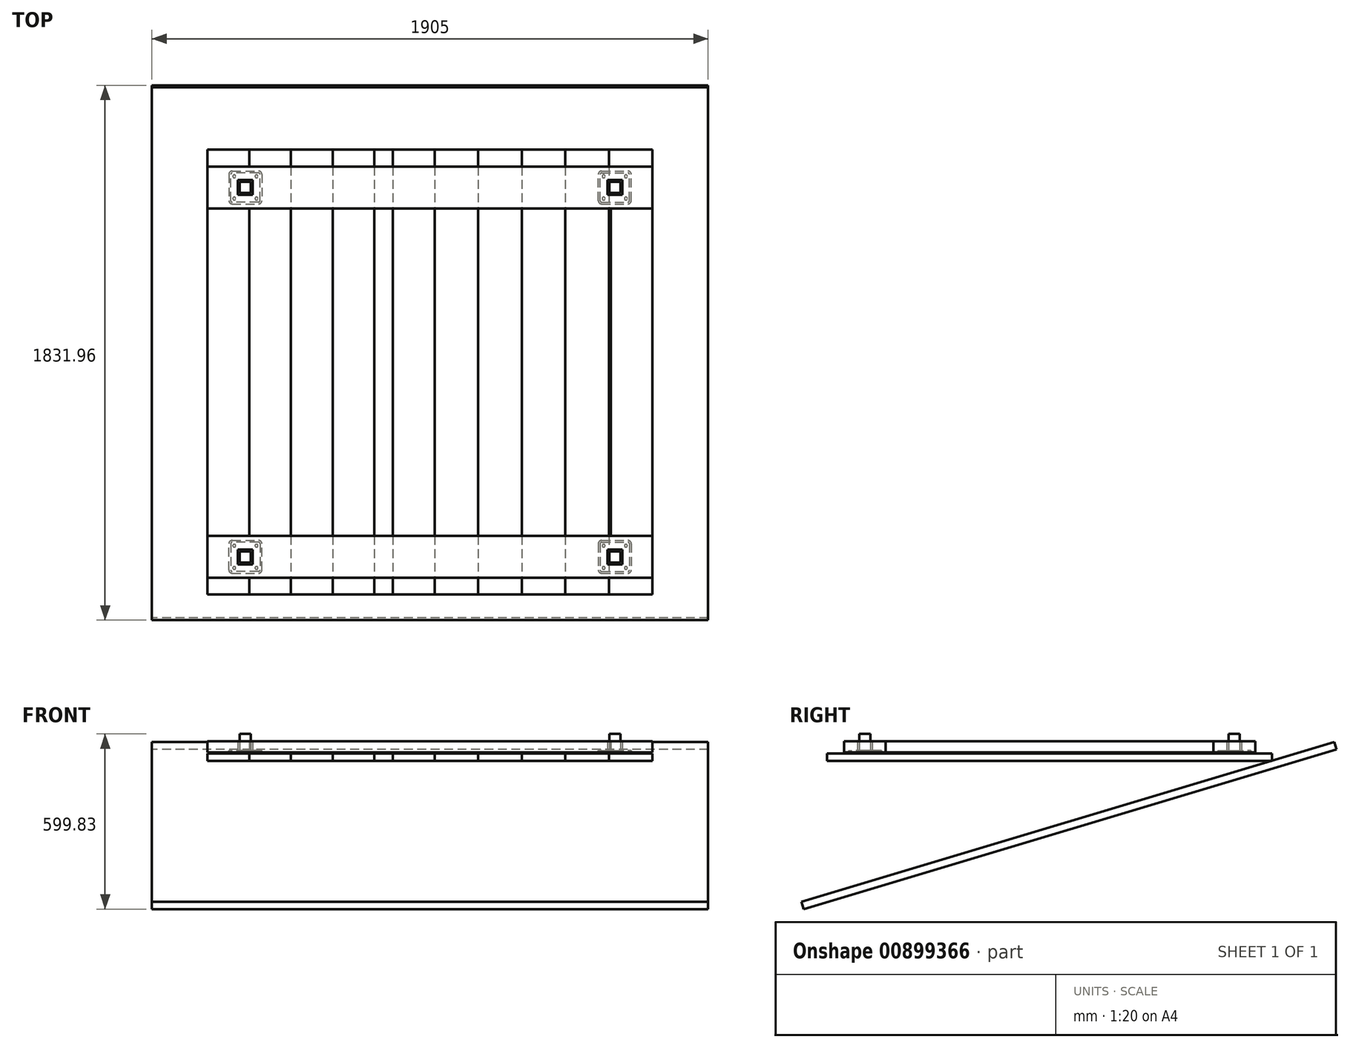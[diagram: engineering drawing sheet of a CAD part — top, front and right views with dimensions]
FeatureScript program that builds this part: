
annotation { "Feature Type Name" : "Feature", "Feature Type Description" : "" }
export const myFeature = defineFeature(function(context is Context, id is Id, definition is map)
    precondition{}
    {
        {
            var Q0;
            Q0=qCreatedBy(makeId("Top.planeOp"),FACE);
            var sketch = newSketch(context, id + "F0", { "sketchPlane" : qUnion([Q0])});
            skLineSegment(sketch, "E0.bottom", {"start": v(762, -762) * mm, "end": v(-762, -762) * mm});
            skLineSegment(sketch, "E0.top", {"start": v(762, 762) * mm, "end": v(-762, 762) * mm});
            skLineSegment(sketch, "E0.left", {"start": v(762, -762) * mm, "end": v(762, 762) * mm});
            skLineSegment(sketch, "E0.right", {"start": v(-762, -762) * mm, "end": v(-762, 762) * mm});
            skPoint(sketch, "E0.middle", {"position": v(0, 0) * mm});
            skLineSegment(sketch, "E1", {"start": v(-619.13, 762) * mm, "end": v(-619.13, -762) * mm});
            skLineSegment(sketch, "E2", {"start": v(612.78, 762) * mm, "end": v(612.78, -762) * mm});
            skLineSegment(sketch, "E3", {"start": v(-476.25, 762) * mm, "end": v(-476.25, -762) * mm});
            skLineSegment(sketch, "E4", {"start": v(-333.38, 762) * mm, "end": v(-333.38, -762) * mm});
            skLineSegment(sketch, "E5", {"start": v(-190.5, 762) * mm, "end": v(-190.5, -762) * mm});
            skLineSegment(sketch, "E6", {"start": v(-127, 762) * mm, "end": v(-127, -762) * mm});
            skLineSegment(sketch, "E7", {"start": v(463.55, 762) * mm, "end": v(463.55, -762) * mm});
            skLineSegment(sketch, "E8", {"start": v(314.33, 762) * mm, "end": v(314.33, -762) * mm});
            skLineSegment(sketch, "E9", {"start": v(165.1, 762) * mm, "end": v(165.1, -762) * mm});
            skLineSegment(sketch, "E10", {"start": v(15.88, 762) * mm, "end": v(15.88, -762) * mm});
            skSolve(sketch);
        }
        {
            var Q0;
            Q0=qCreatedBy(makeId("Right.planeOp"),FACE);
            var sketch = newSketch(context, id + "F1", { "sketchPlane" : qUnion([Q0])});
            skLineSegment(sketch, "E11", {"start": v(762, 0) * mm, "end": v(-762, -457.2) * mm});
            skSolve(sketch);
        }
        {
            var Q0;
            Q0=sQuery(id+"F1.wireOp",EDGE,"E11");
            cPlane(context, id + "F2", {"entities" : qUnion([Q0]), "cplaneType" : CPlaneType.LINE_ANGLE, "offset" : 25.4 * mm, "angle" : 0 * degree, "width" : 152.4 * mm, "height" : 152.4 * mm});
        }
        {
            var Q0;
            Q0=qCreatedBy(id+"F2.planeOp",FACE);
            var sketch = newSketch(context, id + "F3", { "sketchPlane" : qUnion([Q0])});
            skLineSegment(sketch, "E12.bottom", {"start": v(952.5, 952.5) * mm, "end": v(-952.5, 952.5) * mm});
            skLineSegment(sketch, "E12.top", {"start": v(952.5, -952.5) * mm, "end": v(-952.5, -952.5) * mm});
            skLineSegment(sketch, "E12.left", {"start": v(952.5, 952.5) * mm, "end": v(952.5, -952.5) * mm});
            skLineSegment(sketch, "E12.right", {"start": v(-952.5, 952.5) * mm, "end": v(-952.5, -952.5) * mm});
            skPoint(sketch, "E12.middle", {"position": v(0, 0) * mm});
            skSolve(sketch);
        }
        {
            var Q0;
            Q0=makeQuery(id+"F3.imprint","IMPRINT",FACE,{"disambiguationData":[TD([[makeQuery(id+"F3.imprint","IMPRINT",EDGE,{"derivedFrom":sQuery(id+"F3.wireOp",EDGE,"E12.bottom")}),1.0]])]});
            extrude(context, id + "F4", {"entities" : qUnion([Q0]), "depth" : 25.4 * mm, "offsetDistance" : 25.4 * mm});
        }
        {
            var Q0;
            {var subQ0=sQuery(id+"F0.wireOp",EDGE,"E1");Q0=makeQuery(id+"F0.imprint","IMPRINT",FACE,{"disambiguationData":[TD([[makeQuery(id+"F0.imprint","IMPRINT",EDGE,{"derivedFrom":subQ0}),1.0]])]});}
            var Q1;
            {var subQ0=sQuery(id+"F0.wireOp",EDGE,"E4");Q1=makeQuery(id+"F0.imprint","IMPRINT",FACE,{"disambiguationData":[TD([[makeQuery(id+"F0.imprint","IMPRINT",EDGE,{"derivedFrom":subQ0}),1.0]])]});}
            var Q2;
            {var subQ0=sQuery(id+"F0.wireOp",EDGE,"E6");Q2=makeQuery(id+"F0.imprint","IMPRINT",FACE,{"disambiguationData":[TD([[makeQuery(id+"F0.imprint","IMPRINT",EDGE,{"derivedFrom":subQ0}),1.0]])]});}
            var Q3;
            {var subQ0=sQuery(id+"F0.wireOp",EDGE,"E8");Q3=makeQuery(id+"F0.imprint","IMPRINT",FACE,{"disambiguationData":[TD([[makeQuery(id+"F0.imprint","IMPRINT",EDGE,{"derivedFrom":subQ0}),-1.0]])]});}
            var Q4;
            {var subQ0=sQuery(id+"F0.wireOp",EDGE,"E2");Q4=makeQuery(id+"F0.imprint","IMPRINT",FACE,{"disambiguationData":[TD([[makeQuery(id+"F0.imprint","IMPRINT",EDGE,{"derivedFrom":subQ0}),-1.0]])]});}
            extrude(context, id + "F5", {"entities" : qUnion([Q0, Q1, Q2, Q3, Q4]), "depth" : 25.4 * mm, "offsetDistance" : 25.4 * mm});
        }
        {
            var Q0;
            {var subQ0=sQuery(id+"F0.wireOp",EDGE,"E0.right");Q0=makeQuery(id+"F0.imprint","IMPRINT",FACE,{"disambiguationData":[TD([[makeQuery(id+"F0.imprint","IMPRINT",EDGE,{"derivedFrom":subQ0}),-1.0]])]});}
            var Q1;
            {var subQ0=sQuery(id+"F0.wireOp",EDGE,"E3");Q1=makeQuery(id+"F0.imprint","IMPRINT",FACE,{"disambiguationData":[TD([[makeQuery(id+"F0.imprint","IMPRINT",EDGE,{"derivedFrom":subQ0}),1.0]])]});}
            var Q2;
            {var subQ0=sQuery(id+"F0.wireOp",EDGE,"E5");Q2=makeQuery(id+"F0.imprint","IMPRINT",FACE,{"disambiguationData":[TD([[makeQuery(id+"F0.imprint","IMPRINT",EDGE,{"derivedFrom":subQ0}),1.0]])]});}
            var Q3;
            {var subQ0=sQuery(id+"F0.wireOp",EDGE,"E9");Q3=makeQuery(id+"F0.imprint","IMPRINT",FACE,{"disambiguationData":[TD([[makeQuery(id+"F0.imprint","IMPRINT",EDGE,{"derivedFrom":subQ0}),-1.0]])]});}
            var Q4;
            {var subQ0=sQuery(id+"F0.wireOp",EDGE,"E7");Q4=makeQuery(id+"F0.imprint","IMPRINT",FACE,{"disambiguationData":[TD([[makeQuery(id+"F0.imprint","IMPRINT",EDGE,{"derivedFrom":subQ0}),-1.0]])]});}
            var Q5;
            {var subQ0=sQuery(id+"F0.wireOp",EDGE,"E0.left");Q5=makeQuery(id+"F0.imprint","IMPRINT",FACE,{"disambiguationData":[TD([[makeQuery(id+"F0.imprint","IMPRINT",EDGE,{"derivedFrom":subQ0}),1.0]])]});}
            extrude(context, id + "F6", {"entities" : qUnion([Q0, Q1, Q2, Q3, Q4, Q5]), "depth" : 25.4 * mm, "offsetDistance" : 25.4 * mm});
        }
        {
            var Q0;
            Q0=qCreatedBy(makeId("Top.planeOp"),FACE);
            cPlane(context, id + "F7", {"entities" : qUnion([Q0]), "cplaneType" : CPlaneType.OFFSET, "offset" : 25.4 * mm, "width" : 152.4 * mm, "height" : 152.4 * mm});
        }
        {
            var Q0;
            Q0=qCreatedBy(id+"F7.planeOp",FACE);
            var sketch = newSketch(context, id + "F8", { "sketchPlane" : qUnion([Q0])});
            skLineSegment(sketch, "E13", {"start": v(-889.17, 0) * mm, "end": v(880.99, 0) * mm, "construction": true});
            skLineSegment(sketch, "E14", {"start": v(0, 851.29) * mm, "end": v(0, -881.65) * mm, "construction": true});
            skLineSegment(sketch, "E15.bottom", {"start": v(-587.38, 582.61) * mm, "end": v(-677.86, 582.61) * mm});
            skLineSegment(sketch, "E15.top", {"start": v(-587.38, 682.62) * mm, "end": v(-677.86, 682.62) * mm});
            skLineSegment(sketch, "E15.left", {"start": v(-582.61, 587.38) * mm, "end": v(-582.61, 677.86) * mm});
            skLineSegment(sketch, "E15.right", {"start": v(-682.62, 587.38) * mm, "end": v(-682.62, 677.86) * mm});
            skPoint(sketch, "E15.middle", {"position": v(-632.62, 632.62) * mm});
            skPoint(sketch, "E16.visualSharp", {"position": v(-682.62, 682.62) * mm});
            skArc(sketch, "E16.filletArc", {"start": v(-677.86, 682.62) * mm, "mid": v(-681.23, 681.23) * mm, "end": v(-682.62, 677.86) * mm});
            skPoint(sketch, "E17.visualSharp", {"position": v(-582.61, 682.62) * mm});
            skArc(sketch, "E17.filletArc", {"start": v(-582.61, 677.86) * mm, "mid": v(-584, 681.23) * mm, "end": v(-587.38, 682.62) * mm});
            skPoint(sketch, "E18.visualSharp", {"position": v(-582.61, 582.61) * mm});
            skArc(sketch, "E18.filletArc", {"start": v(-587.38, 582.61) * mm, "mid": v(-584, 584) * mm, "end": v(-582.61, 587.38) * mm});
            skPoint(sketch, "E19.visualSharp", {"position": v(-682.62, 582.61) * mm});
            skArc(sketch, "E19.filletArc", {"start": v(-682.62, 587.38) * mm, "mid": v(-681.23, 584) * mm, "end": v(-677.86, 582.61) * mm});
            skCircle(sketch, "E20", {"center": v(-670.72, 670.72) * mm, "radius": 5.08 * mm});
            skCircle(sketch, "E21", {"center": v(-594.52, 670.72) * mm, "radius": 5.08 * mm});
            skCircle(sketch, "E22", {"center": v(-594.52, 594.52) * mm, "radius": 5.08 * mm});
            skCircle(sketch, "E23", {"center": v(-670.72, 594.52) * mm, "radius": 5.08 * mm});
            skLineSegment(sketch, "E24", {"start": v(-686.43, 632.62) * mm, "end": v(-578.8, 632.62) * mm, "construction": true});
            skLineSegment(sketch, "E25", {"start": v(-632.62, 682.62) * mm, "end": v(-632.62, 582.61) * mm, "construction": true});
            skLineSegment(sketch, "E26", {"start": v(-670.72, 594.52) * mm, "end": v(-594.52, 594.52) * mm, "construction": true});
            skLineSegment(sketch, "E27", {"start": v(-670.72, 594.52) * mm, "end": v(-670.72, 670.72) * mm, "construction": true});
            skPoint(sketch, "E28", {"position": v(-670.72, 632.62) * mm});
            skPoint(sketch, "E29", {"position": v(-632.62, 594.52) * mm});
            skLineSegment(sketch, "E30", {"start": v(-632.62, -632.62) * mm, "end": v(632.62, -632.62) * mm, "construction": true});
            skLineSegment(sketch, "E31.bottom", {"start": v(677.86, 582.61) * mm, "end": v(587.38, 582.61) * mm});
            skLineSegment(sketch, "E31.top", {"start": v(677.86, 682.62) * mm, "end": v(587.38, 682.62) * mm});
            skLineSegment(sketch, "E31.left", {"start": v(682.63, 587.38) * mm, "end": v(682.63, 677.86) * mm});
            skLineSegment(sketch, "E31.right", {"start": v(582.61, 587.38) * mm, "end": v(582.61, 677.86) * mm});
            skPoint(sketch, "E31.middle", {"position": v(632.62, 632.62) * mm});
            skPoint(sketch, "E32.visualSharp", {"position": v(582.61, 682.62) * mm});
            skArc(sketch, "E32.filletArc", {"start": v(587.38, 682.62) * mm, "mid": v(584, 681.23) * mm, "end": v(582.61, 677.86) * mm});
            skPoint(sketch, "E33.visualSharp", {"position": v(682.63, 682.62) * mm});
            skArc(sketch, "E33.filletArc", {"start": v(682.63, 677.86) * mm, "mid": v(681.23, 681.23) * mm, "end": v(677.86, 682.62) * mm});
            skPoint(sketch, "E34.visualSharp", {"position": v(682.63, 582.61) * mm});
            skArc(sketch, "E34.filletArc", {"start": v(677.86, 582.61) * mm, "mid": v(681.23, 584) * mm, "end": v(682.63, 587.38) * mm});
            skPoint(sketch, "E35.visualSharp", {"position": v(582.61, 582.61) * mm});
            skArc(sketch, "E35.filletArc", {"start": v(582.61, 587.38) * mm, "mid": v(584, 584) * mm, "end": v(587.38, 582.61) * mm});
            skCircle(sketch, "E36", {"center": v(594.52, 670.72) * mm, "radius": 5.08 * mm});
            skCircle(sketch, "E37", {"center": v(670.72, 670.72) * mm, "radius": 5.08 * mm});
            skCircle(sketch, "E38", {"center": v(670.72, 594.52) * mm, "radius": 5.08 * mm});
            skCircle(sketch, "E39", {"center": v(594.52, 594.52) * mm, "radius": 5.08 * mm});
            skLineSegment(sketch, "E40", {"start": v(582.61, 632.62) * mm, "end": v(682.62, 632.62) * mm, "construction": true});
            skLineSegment(sketch, "E41", {"start": v(632.62, 682.62) * mm, "end": v(632.62, 582.61) * mm, "construction": true});
            skLineSegment(sketch, "E42", {"start": v(594.52, 594.52) * mm, "end": v(670.72, 594.52) * mm, "construction": true});
            skLineSegment(sketch, "E43", {"start": v(594.52, 594.52) * mm, "end": v(594.52, 670.72) * mm, "construction": true});
            skPoint(sketch, "E44", {"position": v(594.52, 632.62) * mm});
            skPoint(sketch, "E45", {"position": v(632.62, 594.52) * mm});
            skLineSegment(sketch, "E46.bottom", {"start": v(-587.38, -682.62) * mm, "end": v(-677.86, -682.62) * mm});
            skLineSegment(sketch, "E46.top", {"start": v(-587.38, -582.61) * mm, "end": v(-677.86, -582.61) * mm});
            skLineSegment(sketch, "E46.left", {"start": v(-582.61, -677.86) * mm, "end": v(-582.61, -587.38) * mm});
            skLineSegment(sketch, "E46.right", {"start": v(-682.62, -677.86) * mm, "end": v(-682.62, -587.38) * mm});
            skPoint(sketch, "E46.middle", {"position": v(-632.62, -632.62) * mm});
            skPoint(sketch, "E47.visualSharp", {"position": v(-682.62, -582.61) * mm});
            skArc(sketch, "E47.filletArc", {"start": v(-677.86, -582.61) * mm, "mid": v(-681.23, -584) * mm, "end": v(-682.62, -587.38) * mm});
            skPoint(sketch, "E48.visualSharp", {"position": v(-582.61, -582.61) * mm});
            skArc(sketch, "E48.filletArc", {"start": v(-582.61, -587.38) * mm, "mid": v(-584, -584) * mm, "end": v(-587.38, -582.61) * mm});
            skPoint(sketch, "E49.visualSharp", {"position": v(-582.61, -682.62) * mm});
            skArc(sketch, "E49.filletArc", {"start": v(-587.38, -682.62) * mm, "mid": v(-584, -681.23) * mm, "end": v(-582.61, -677.86) * mm});
            skPoint(sketch, "E50.visualSharp", {"position": v(-682.62, -682.62) * mm});
            skArc(sketch, "E50.filletArc", {"start": v(-682.62, -677.86) * mm, "mid": v(-681.23, -681.23) * mm, "end": v(-677.86, -682.62) * mm});
            skCircle(sketch, "E51", {"center": v(-670.72, -594.52) * mm, "radius": 5.08 * mm});
            skCircle(sketch, "E52", {"center": v(-594.52, -594.52) * mm, "radius": 5.08 * mm});
            skCircle(sketch, "E53", {"center": v(-594.52, -670.72) * mm, "radius": 5.08 * mm});
            skCircle(sketch, "E54", {"center": v(-670.72, -670.72) * mm, "radius": 5.08 * mm});
            skLineSegment(sketch, "E55", {"start": v(-682.62, -632.62) * mm, "end": v(-582.61, -632.62) * mm, "construction": true});
            skLineSegment(sketch, "E56", {"start": v(-632.62, -582.61) * mm, "end": v(-632.62, -682.62) * mm, "construction": true});
            skLineSegment(sketch, "E57", {"start": v(-670.72, -670.72) * mm, "end": v(-594.52, -670.72) * mm, "construction": true});
            skLineSegment(sketch, "E58", {"start": v(-670.72, -670.72) * mm, "end": v(-670.72, -594.52) * mm, "construction": true});
            skPoint(sketch, "E59", {"position": v(-670.72, -632.62) * mm});
            skPoint(sketch, "E60", {"position": v(-632.62, -670.72) * mm});
            skLineSegment(sketch, "E61.bottom", {"start": v(677.86, -682.62) * mm, "end": v(587.38, -682.62) * mm});
            skLineSegment(sketch, "E61.top", {"start": v(677.86, -582.61) * mm, "end": v(587.38, -582.61) * mm});
            skLineSegment(sketch, "E61.left", {"start": v(682.62, -677.86) * mm, "end": v(682.62, -587.38) * mm});
            skLineSegment(sketch, "E61.right", {"start": v(582.61, -677.86) * mm, "end": v(582.61, -587.38) * mm});
            skPoint(sketch, "E61.middle", {"position": v(632.62, -632.62) * mm});
            skPoint(sketch, "E62.visualSharp", {"position": v(582.61, -582.61) * mm});
            skArc(sketch, "E62.filletArc", {"start": v(587.38, -582.61) * mm, "mid": v(584, -584) * mm, "end": v(582.61, -587.38) * mm});
            skPoint(sketch, "E63.visualSharp", {"position": v(682.62, -582.61) * mm});
            skArc(sketch, "E63.filletArc", {"start": v(682.62, -587.38) * mm, "mid": v(681.23, -584) * mm, "end": v(677.86, -582.61) * mm});
            skPoint(sketch, "E64.visualSharp", {"position": v(682.62, -682.62) * mm});
            skArc(sketch, "E64.filletArc", {"start": v(677.86, -682.62) * mm, "mid": v(681.23, -681.23) * mm, "end": v(682.62, -677.86) * mm});
            skPoint(sketch, "E65.visualSharp", {"position": v(582.61, -682.62) * mm});
            skArc(sketch, "E65.filletArc", {"start": v(582.61, -677.86) * mm, "mid": v(584, -681.23) * mm, "end": v(587.38, -682.62) * mm});
            skCircle(sketch, "E66", {"center": v(594.52, -594.52) * mm, "radius": 5.08 * mm});
            skCircle(sketch, "E67", {"center": v(670.72, -594.52) * mm, "radius": 5.08 * mm});
            skCircle(sketch, "E68", {"center": v(670.72, -670.72) * mm, "radius": 5.08 * mm});
            skCircle(sketch, "E69", {"center": v(594.52, -670.72) * mm, "radius": 5.08 * mm});
            skLineSegment(sketch, "E70", {"start": v(582.61, -632.62) * mm, "end": v(682.62, -632.62) * mm, "construction": true});
            skLineSegment(sketch, "E71", {"start": v(632.62, -594.52) * mm, "end": v(632.62, -670.72) * mm, "construction": true});
            skLineSegment(sketch, "E72", {"start": v(594.52, -670.72) * mm, "end": v(670.72, -670.72) * mm, "construction": true});
            skLineSegment(sketch, "E73", {"start": v(594.52, -670.72) * mm, "end": v(594.52, -594.52) * mm, "construction": true});
            skPoint(sketch, "E74", {"position": v(594.52, -632.62) * mm});
            skPoint(sketch, "E75", {"position": v(632.62, -670.72) * mm});
            skPoint(sketch, "E76", {"position": v(0, -632.62) * mm});
            skLineSegment(sketch, "E77", {"start": v(-632.62, -632.62) * mm, "end": v(-632.62, 632.62) * mm, "construction": true});
            skPoint(sketch, "E78", {"position": v(-632.62, 0) * mm});
            skSolve(sketch);
        }
        {
            var Q0;
            Q0=makeQuery(id+"F8.imprint","IMPRINT",FACE,{"disambiguationData":[TD([[makeQuery(id+"F8.imprint","IMPRINT",EDGE,{"derivedFrom":sQuery(id+"F8.wireOp",EDGE,"E15.bottom")}),-1.0]])]});
            extrude(context, id + "F9", {"entities" : qUnion([Q0]), "depth" : 3.17 * mm, "offsetDistance" : 25.4 * mm});
        }
        {
            var Q0;
            Q0=makeQuery(id+"F9.opExtrude","CAP_FACE",FACE,{"disambiguationData":[OSD([sQuery(id+"F8.wireOp",EDGE,"E15.bottom"),sQuery(id+"F8.wireOp",EDGE,"E15.top"),sQuery(id+"F8.wireOp",EDGE,"E15.left"),sQuery(id+"F8.wireOp",EDGE,"E15.right"),sQuery(id+"F8.wireOp",EDGE,"E16.filletArc"),sQuery(id+"F8.wireOp",EDGE,"E17.filletArc"),sQuery(id+"F8.wireOp",EDGE,"E18.filletArc"),sQuery(id+"F8.wireOp",EDGE,"E19.filletArc"),sQuery(id+"F8.wireOp",EDGE,"E20"),sQuery(id+"F8.wireOp",EDGE,"E21"),sQuery(id+"F8.wireOp",EDGE,"E22"),sQuery(id+"F8.wireOp",EDGE,"E23")])],"isStart":false});
            var sketch = newSketch(context, id + "F10", { "sketchPlane" : qUnion([Q0])});
            skLineSegment(sketch, "E79.bottom", {"start": v(-613.57, 613.57) * mm, "end": v(-651.67, 613.57) * mm});
            skLineSegment(sketch, "E79.top", {"start": v(-613.57, 651.67) * mm, "end": v(-651.67, 651.67) * mm});
            skLineSegment(sketch, "E79.left", {"start": v(-613.57, 613.57) * mm, "end": v(-613.57, 651.67) * mm});
            skLineSegment(sketch, "E79.right", {"start": v(-651.67, 613.57) * mm, "end": v(-651.67, 651.67) * mm});
            skPoint(sketch, "E79.middle", {"position": v(-632.62, 632.62) * mm});
            skLineSegment(sketch, "E80", {"start": v(-632.62, 682.62) * mm, "end": v(-632.62, 582.61) * mm, "construction": true});
            skLineSegment(sketch, "E81", {"start": v(-582.61, 632.62) * mm, "end": v(-682.62, 632.62) * mm, "construction": true});
            skLineSegment(sketch, "E82.0", {"start": v(-648.5, 616.74) * mm, "end": v(-648.5, 648.5) * mm});
            skLineSegment(sketch, "E82.1", {"start": v(-616.74, 616.74) * mm, "end": v(-648.5, 616.74) * mm});
            skLineSegment(sketch, "E82.2", {"start": v(-616.74, 616.74) * mm, "end": v(-616.74, 648.5) * mm});
            skLineSegment(sketch, "E82.3", {"start": v(-616.74, 648.5) * mm, "end": v(-648.5, 648.5) * mm});
            skSolve(sketch);
        }
        {
            var Q0;
            Q0 = qSketchRegion(id + "F10", true);
            var Q1;
            Q1=makeQuery(id+"F10.imprint","IMPRINT",FACE,{"disambiguationData":[TD([[makeQuery(id+"F10.imprint","IMPRINT",EDGE,{"derivedFrom":sQuery(id+"F10.wireOp",EDGE,"E82.0")}),-1.0]])]});
            extrude(context, id + "F11", {"entities" : qUnion([Q0, Q1]), "operationType" : NewBodyOperationType.ADD, "depth" : 63.5 * mm, "offsetDistance" : 25.4 * mm});
        }
        {
            var Q0;
            Q0=makeQuery(id+"F9.opExtrude","SWEPT_BODY",BODY,{"disambiguationData":[OSD([sQuery(id+"F8.wireOp",EDGE,"E15.bottom"),sQuery(id+"F8.wireOp",EDGE,"E15.top"),sQuery(id+"F8.wireOp",EDGE,"E15.left"),sQuery(id+"F8.wireOp",EDGE,"E15.right"),sQuery(id+"F8.wireOp",EDGE,"E16.filletArc"),sQuery(id+"F8.wireOp",EDGE,"E17.filletArc"),sQuery(id+"F8.wireOp",EDGE,"E18.filletArc"),sQuery(id+"F8.wireOp",EDGE,"E19.filletArc"),sQuery(id+"F8.wireOp",EDGE,"E20"),sQuery(id+"F8.wireOp",EDGE,"E21"),sQuery(id+"F8.wireOp",EDGE,"E22"),sQuery(id+"F8.wireOp",EDGE,"E23")])]});
            var Q1;
            Q1=qCreatedBy(makeId("Right.planeOp"),FACE);
            mirror(context, id + "F12", {"entities" : qUnion([Q0]), "mirrorPlane" : qUnion([Q1])});
        }
        {
            var Q0;
            Q0=makeQuery(id+"F9.opExtrude","CAP_FACE",FACE,{"disambiguationData":[OSD([sQuery(id+"F8.wireOp",EDGE,"E15.bottom"),sQuery(id+"F8.wireOp",EDGE,"E15.top"),sQuery(id+"F8.wireOp",EDGE,"E15.left"),sQuery(id+"F8.wireOp",EDGE,"E15.right"),sQuery(id+"F8.wireOp",EDGE,"E16.filletArc"),sQuery(id+"F8.wireOp",EDGE,"E17.filletArc"),sQuery(id+"F8.wireOp",EDGE,"E18.filletArc"),sQuery(id+"F8.wireOp",EDGE,"E19.filletArc"),sQuery(id+"F8.wireOp",EDGE,"E20"),sQuery(id+"F8.wireOp",EDGE,"E21"),sQuery(id+"F8.wireOp",EDGE,"E22"),sQuery(id+"F8.wireOp",EDGE,"E23")])],"isStart":false});
            cPlane(context, id + "F13", {"entities" : qUnion([Q0]), "cplaneType" : CPlaneType.OFFSET, "offset" : 0 * mm, "width" : 152.4 * mm, "height" : 152.4 * mm});
        }
        {
            var Q0;
            Q0=qCreatedBy(id+"F13.planeOp",FACE);
            var sketch = newSketch(context, id + "F14", { "sketchPlane" : qUnion([Q0])});
            skLineSegment(sketch, "E83.bottom", {"start": v(-762, 704.06) * mm, "end": v(762, 704.06) * mm});
            skLineSegment(sketch, "E83.top", {"start": v(-762, 561.18) * mm, "end": v(762, 561.18) * mm});
            skLineSegment(sketch, "E83.left", {"start": v(-762, 704.06) * mm, "end": v(-762, 561.18) * mm});
            skLineSegment(sketch, "E83.right", {"start": v(762, 704.06) * mm, "end": v(762, 561.18) * mm});
            skPoint(sketch, "E84", {"position": v(-682.62, 632.62) * mm});
            skPoint(sketch, "E85", {"position": v(682.62, 632.62) * mm});
            skPoint(sketch, "E86", {"position": v(0, 632.62) * mm});
            skPoint(sketch, "E87.positionSnap0", {"position": v(0, 704.06) * mm});
            skPoint(sketch, "E87.positionSnap1", {"position": v(-762, 632.62) * mm});
            skSolve(sketch);
        }
        {
            var Q0;
            Q0 = qSketchRegion(id + "F14", true);
            extrude(context, id + "F15", {"entities" : qUnion([Q0]), "depth" : 38.1 * mm, "offsetDistance" : 25.4 * mm});
        }
        {
            var Q0;
            Q0=makeQuery(id+"F9.opExtrude","SWEPT_BODY",BODY,{"disambiguationData":[OSD([sQuery(id+"F8.wireOp",EDGE,"E15.bottom"),sQuery(id+"F8.wireOp",EDGE,"E15.top"),sQuery(id+"F8.wireOp",EDGE,"E15.left"),sQuery(id+"F8.wireOp",EDGE,"E15.right"),sQuery(id+"F8.wireOp",EDGE,"E16.filletArc"),sQuery(id+"F8.wireOp",EDGE,"E17.filletArc"),sQuery(id+"F8.wireOp",EDGE,"E18.filletArc"),sQuery(id+"F8.wireOp",EDGE,"E19.filletArc"),sQuery(id+"F8.wireOp",EDGE,"E20"),sQuery(id+"F8.wireOp",EDGE,"E21"),sQuery(id+"F8.wireOp",EDGE,"E22"),sQuery(id+"F8.wireOp",EDGE,"E23")])]});
            var Q1;
            Q1=makeQuery(id+"F12.opPattern","COPY",BODY,{"derivedFrom":makeQuery(id+"F9.opExtrude","SWEPT_BODY",BODY,{"disambiguationData":[OSD([sQuery(id+"F8.wireOp",EDGE,"E15.bottom"),sQuery(id+"F8.wireOp",EDGE,"E15.top"),sQuery(id+"F8.wireOp",EDGE,"E15.left"),sQuery(id+"F8.wireOp",EDGE,"E15.right"),sQuery(id+"F8.wireOp",EDGE,"E16.filletArc"),sQuery(id+"F8.wireOp",EDGE,"E17.filletArc"),sQuery(id+"F8.wireOp",EDGE,"E18.filletArc"),sQuery(id+"F8.wireOp",EDGE,"E19.filletArc"),sQuery(id+"F8.wireOp",EDGE,"E20"),sQuery(id+"F8.wireOp",EDGE,"E21"),sQuery(id+"F8.wireOp",EDGE,"E22"),sQuery(id+"F8.wireOp",EDGE,"E23")])]}),"instanceName":"1"});
            var Q2;
            Q2=makeQuery(id+"F15.opExtrude","SWEPT_BODY",BODY,{"disambiguationData":[OSD([sQuery(id+"F14.wireOp",EDGE,"E83.bottom"),sQuery(id+"F14.wireOp",EDGE,"E83.top"),sQuery(id+"F14.wireOp",EDGE,"E83.left"),sQuery(id+"F14.wireOp",EDGE,"E83.right")])]});
            booleanBodies(context, id + "F16", {"operationType" : BooleanOperationType.SUBTRACTION, "tools" : qUnion([Q0, Q1]), "targets" : qUnion([Q2]), "offset" : true, "offsetAll" : true, "offsetDistance" : 6.35 * mm, "keepTools" : true});
        }
        {
            var Q0;
            Q0=makeQuery(id+"F9.opExtrude","SWEPT_BODY",BODY,{"disambiguationData":[OSD([sQuery(id+"F8.wireOp",EDGE,"E15.bottom"),sQuery(id+"F8.wireOp",EDGE,"E15.top"),sQuery(id+"F8.wireOp",EDGE,"E15.left"),sQuery(id+"F8.wireOp",EDGE,"E15.right"),sQuery(id+"F8.wireOp",EDGE,"E16.filletArc"),sQuery(id+"F8.wireOp",EDGE,"E17.filletArc"),sQuery(id+"F8.wireOp",EDGE,"E18.filletArc"),sQuery(id+"F8.wireOp",EDGE,"E19.filletArc"),sQuery(id+"F8.wireOp",EDGE,"E20"),sQuery(id+"F8.wireOp",EDGE,"E21"),sQuery(id+"F8.wireOp",EDGE,"E22"),sQuery(id+"F8.wireOp",EDGE,"E23")])]});
            var Q1;
            Q1=makeQuery(id+"F12.opPattern","COPY",BODY,{"derivedFrom":makeQuery(id+"F9.opExtrude","SWEPT_BODY",BODY,{"disambiguationData":[OSD([sQuery(id+"F8.wireOp",EDGE,"E15.bottom"),sQuery(id+"F8.wireOp",EDGE,"E15.top"),sQuery(id+"F8.wireOp",EDGE,"E15.left"),sQuery(id+"F8.wireOp",EDGE,"E15.right"),sQuery(id+"F8.wireOp",EDGE,"E16.filletArc"),sQuery(id+"F8.wireOp",EDGE,"E17.filletArc"),sQuery(id+"F8.wireOp",EDGE,"E18.filletArc"),sQuery(id+"F8.wireOp",EDGE,"E19.filletArc"),sQuery(id+"F8.wireOp",EDGE,"E20"),sQuery(id+"F8.wireOp",EDGE,"E21"),sQuery(id+"F8.wireOp",EDGE,"E22"),sQuery(id+"F8.wireOp",EDGE,"E23")])]}),"instanceName":"1"});
            var Q2;
            Q2=makeQuery(id+"F15.opExtrude","SWEPT_BODY",BODY,{"disambiguationData":[OSD([sQuery(id+"F14.wireOp",EDGE,"E83.bottom"),sQuery(id+"F14.wireOp",EDGE,"E83.top"),sQuery(id+"F14.wireOp",EDGE,"E83.left"),sQuery(id+"F14.wireOp",EDGE,"E83.right")])]});
            var Q3;
            Q3=qCreatedBy(makeId("Front.planeOp"),FACE);
            mirror(context, id + "F17", {"entities" : qUnion([Q0, Q1, Q2]), "mirrorPlane" : qUnion([Q3])});
        }
        {
            var Q0;
            Q0=qCreatedBy(id+"F13.planeOp",FACE);
            var sketch = newSketch(context, id + "F18", { "sketchPlane" : qUnion([Q0])});
            skLineSegment(sketch, "E88.bottom", {"start": v(-762, 561.18) * mm, "end": v(-619.13, 561.18) * mm});
            skLineSegment(sketch, "E88.top", {"start": v(-762, -561.18) * mm, "end": v(-619.13, -561.18) * mm});
            skLineSegment(sketch, "E88.left", {"start": v(-762, 561.18) * mm, "end": v(-762, -561.18) * mm});
            skLineSegment(sketch, "E88.right", {"start": v(-619.13, 561.18) * mm, "end": v(-619.13, -561.18) * mm});
            skSolve(sketch);
        }
        {
            var Q0;
            Q0 = qSketchRegion(id + "F18", true);
            extrude(context, id + "F19", {"entities" : qUnion([Q0]), "depth" : 38.1 * mm, "offsetDistance" : 25.4 * mm});
        }
        {
            var Q0;
            Q0=makeQuery(id+"F19.opExtrude","SWEPT_BODY",BODY,{"disambiguationData":[OSD([sQuery(id+"F18.wireOp",EDGE,"E88.bottom"),sQuery(id+"F18.wireOp",EDGE,"E88.top"),sQuery(id+"F18.wireOp",EDGE,"E88.left"),sQuery(id+"F18.wireOp",EDGE,"E88.right")])]});
            var Q1;
            Q1=qCreatedBy(makeId("Right.planeOp"),FACE);
            mirror(context, id + "F20", {"entities" : qUnion([Q0]), "mirrorPlane" : qUnion([Q1])});
        }
    });
